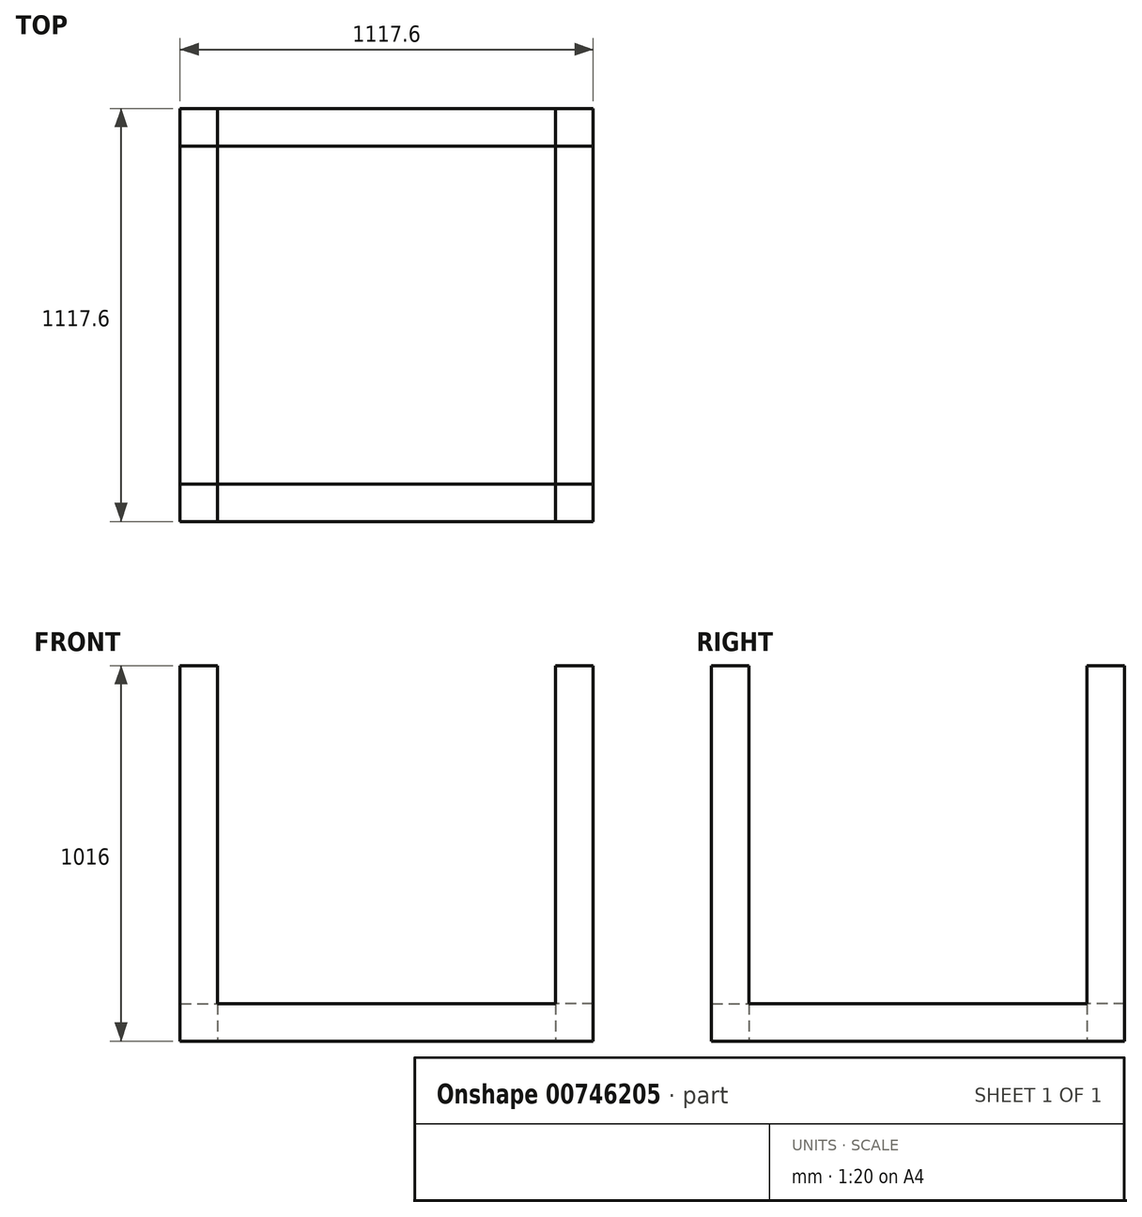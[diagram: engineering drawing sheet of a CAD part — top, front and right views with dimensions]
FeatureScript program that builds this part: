
annotation { "Feature Type Name" : "Feature", "Feature Type Description" : "" }
export const myFeature = defineFeature(function(context is Context, id is Id, definition is map)
    precondition{}
    {
        {
            var Q0;
            Q0=qCreatedBy(makeId("Top.planeOp"),FACE);
            var sketch = newSketch(context, id + "F0", { "sketchPlane" : qUnion([Q0])});
            skLineSegment(sketch, "E0.bottom", {"start": v(457.2, -457.2) * mm, "end": v(-457.2, -457.2) * mm});
            skLineSegment(sketch, "E0.top", {"start": v(457.2, 457.2) * mm, "end": v(-457.2, 457.2) * mm});
            skLineSegment(sketch, "E0.left", {"start": v(457.2, -457.2) * mm, "end": v(457.2, 457.2) * mm});
            skLineSegment(sketch, "E0.right", {"start": v(-457.2, -457.2) * mm, "end": v(-457.2, 457.2) * mm});
            skPoint(sketch, "E0.middle", {"position": v(0, 0) * mm});
            skLineSegment(sketch, "E1.bottom", {"start": v(558.8, -558.8) * mm, "end": v(-558.8, -558.8) * mm});
            skLineSegment(sketch, "E1.top", {"start": v(558.8, 558.8) * mm, "end": v(-558.8, 558.8) * mm});
            skLineSegment(sketch, "E1.left", {"start": v(558.8, -558.8) * mm, "end": v(558.8, 558.8) * mm});
            skLineSegment(sketch, "E1.right", {"start": v(-558.8, -558.8) * mm, "end": v(-558.8, 558.8) * mm});
            skSolve(sketch);
        }
        {
            var Q0;
            Q0 = qSketchRegion(id + "F0", true);
            extrude(context, id + "F1", {"entities" : qUnion([Q0]), "depth" : 101.6 * mm, "offsetDistance" : 25.4 * mm});
        }
        {
            var Q0;
            Q0=makeQuery(id+"F1.opExtrude","CAP_FACE",FACE,{"disambiguationData":[OSD([sQuery(id+"F0.wireOp",EDGE,"E0.bottom"),sQuery(id+"F0.wireOp",EDGE,"E0.top"),sQuery(id+"F0.wireOp",EDGE,"E0.left"),sQuery(id+"F0.wireOp",EDGE,"E0.right"),sQuery(id+"F0.wireOp",EDGE,"E1.bottom"),sQuery(id+"F0.wireOp",EDGE,"E1.top"),sQuery(id+"F0.wireOp",EDGE,"E1.left"),sQuery(id+"F0.wireOp",EDGE,"E1.right")])],"isStart":false});
            var sketch = newSketch(context, id + "F2", { "sketchPlane" : qUnion([Q0])});
            skLineSegment(sketch, "E2.bottom", {"start": v(-457.2, 457.2) * mm, "end": v(-558.8, 457.2) * mm});
            skLineSegment(sketch, "E2.top", {"start": v(-457.2, 558.8) * mm, "end": v(-558.8, 558.8) * mm});
            skLineSegment(sketch, "E2.left", {"start": v(-457.2, 457.2) * mm, "end": v(-457.2, 558.8) * mm});
            skLineSegment(sketch, "E2.right", {"start": v(-558.8, 457.2) * mm, "end": v(-558.8, 558.8) * mm});
            skLineSegment(sketch, "E3.bottom", {"start": v(558.8, 558.8) * mm, "end": v(457.2, 558.8) * mm});
            skLineSegment(sketch, "E3.top", {"start": v(558.8, 457.2) * mm, "end": v(457.2, 457.2) * mm});
            skLineSegment(sketch, "E3.left", {"start": v(558.8, 558.8) * mm, "end": v(558.8, 457.2) * mm});
            skLineSegment(sketch, "E3.right", {"start": v(457.2, 558.8) * mm, "end": v(457.2, 457.2) * mm});
            skLineSegment(sketch, "E4.bottom", {"start": v(558.8, -558.8) * mm, "end": v(457.2, -558.8) * mm});
            skLineSegment(sketch, "E4.top", {"start": v(558.8, -457.2) * mm, "end": v(457.2, -457.2) * mm});
            skLineSegment(sketch, "E4.left", {"start": v(558.8, -558.8) * mm, "end": v(558.8, -457.2) * mm});
            skLineSegment(sketch, "E4.right", {"start": v(457.2, -558.8) * mm, "end": v(457.2, -457.2) * mm});
            skLineSegment(sketch, "E5.bottom", {"start": v(-558.8, -558.8) * mm, "end": v(-457.2, -558.8) * mm});
            skLineSegment(sketch, "E5.top", {"start": v(-558.8, -457.2) * mm, "end": v(-457.2, -457.2) * mm});
            skLineSegment(sketch, "E5.left", {"start": v(-558.8, -558.8) * mm, "end": v(-558.8, -457.2) * mm});
            skLineSegment(sketch, "E5.right", {"start": v(-457.2, -558.8) * mm, "end": v(-457.2, -457.2) * mm});
            skSolve(sketch);
        }
        {
            var Q0;
            Q0 = qSketchRegion(id + "F2", true);
            extrude(context, id + "F3", {"entities" : qUnion([Q0]), "operationType" : NewBodyOperationType.ADD, "depth" : 914.4 * mm, "offsetDistance" : 25.4 * mm});
        }
    });
